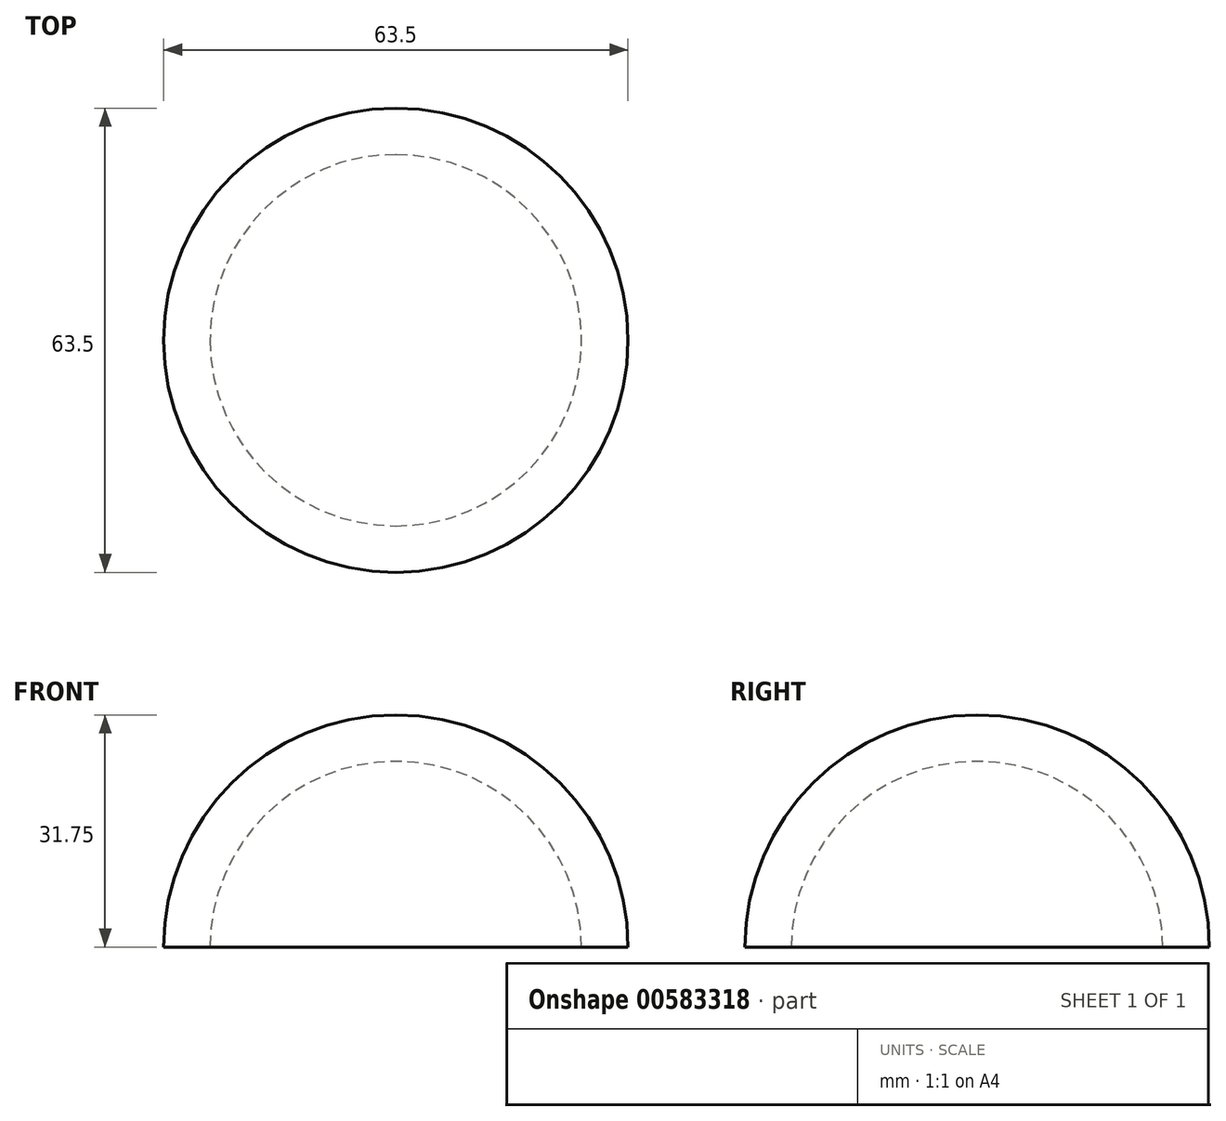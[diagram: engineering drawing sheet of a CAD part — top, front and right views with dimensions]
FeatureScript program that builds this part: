
annotation { "Feature Type Name" : "Feature", "Feature Type Description" : "" }
export const myFeature = defineFeature(function(context is Context, id is Id, definition is map)
    precondition{}
    {
        {
            var Q0;
            Q0=qCreatedBy(makeId("Top.planeOp"),FACE);
            var sketch = newSketch(context, id + "F0", { "sketchPlane" : qUnion([Q0])});
            skCircle(sketch, "E0", {"center": v(0, 0) * mm, "radius": 31.75 * mm});
            skLineSegment(sketch, "E1", {"start": v(0, 31.75) * mm, "end": v(0, -31.75) * mm});
            skCircle(sketch, "E2", {"center": v(0, 0) * mm, "radius": 25.4 * mm});
            skSolve(sketch);
        }
        {
            var Q0;
            {var subQ0=sQuery(id+"F0.wireOp",EDGE,"E1");Q0=makeQuery(id+"F0.imprint","IMPRINT",FACE,{"disambiguationData":[TD([[makeQuery(id+"F0.imprint","IMPRINT",EDGE,{"derivedFrom":subQ0}),1.0]])]});}
            var Q1;
            Q1=sQuery(id+"F0.wireOp",EDGE,"E1");
            revolve(context, id + "F1", {"entities" : qUnion([Q0]), "axis" : qUnion([Q1]), "revolveType" : RevolveType.ONE_DIRECTION, "angle" : 180 * degree});
        }
    });
